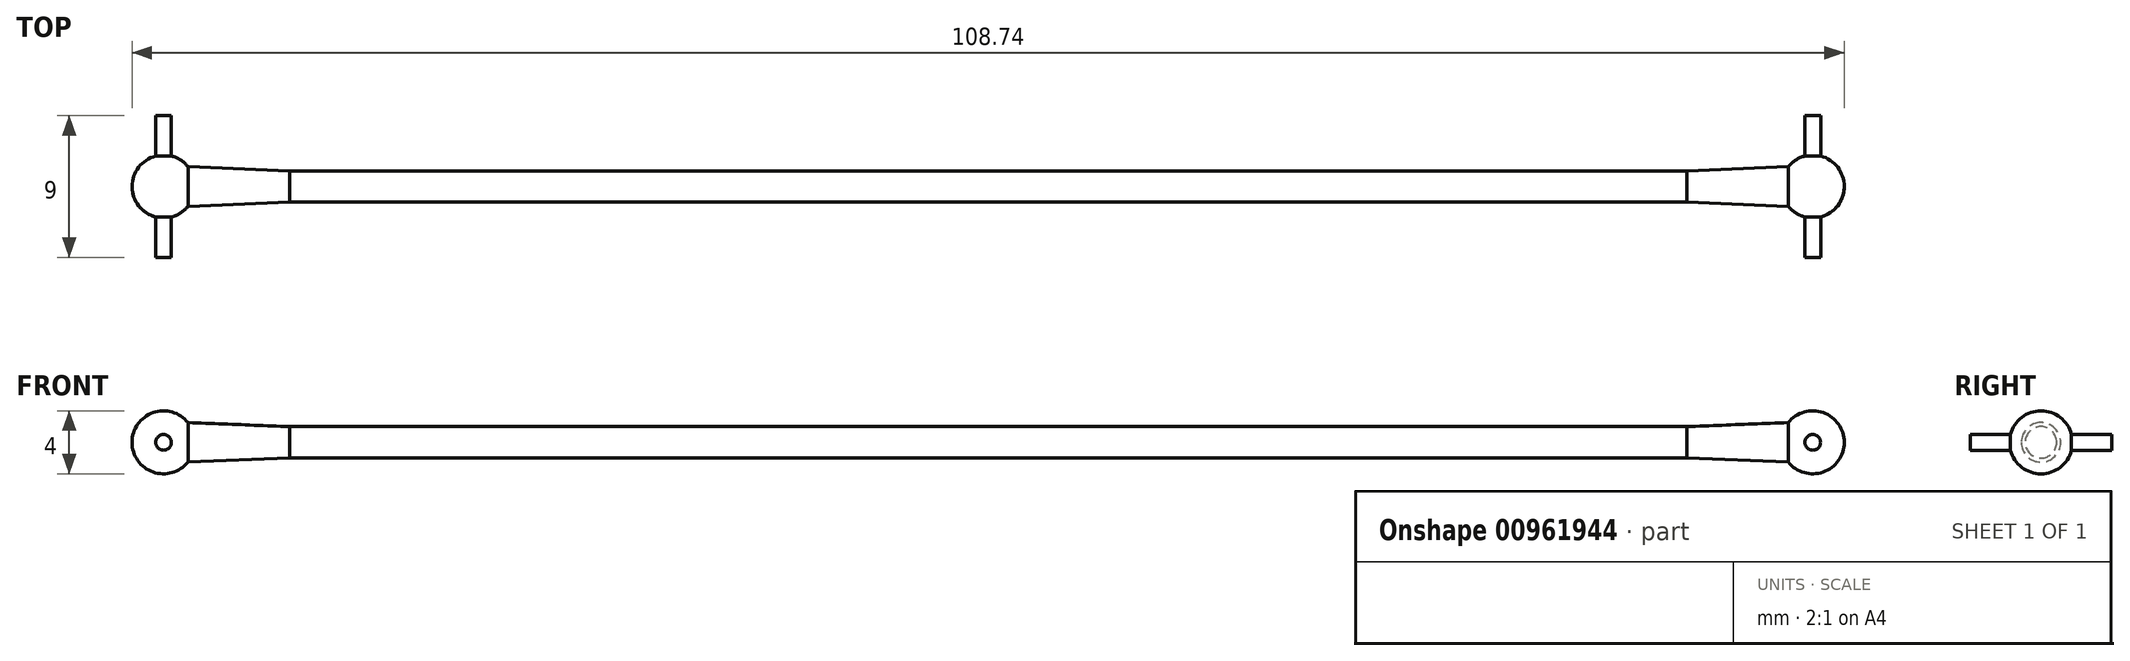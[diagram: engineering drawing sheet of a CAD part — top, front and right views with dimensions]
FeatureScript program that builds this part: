
annotation { "Feature Type Name" : "Feature", "Feature Type Description" : "" }
export const myFeature = defineFeature(function(context is Context, id is Id, definition is map)
    precondition{}
    {
        {
            var Q0;
            Q0=qCreatedBy(makeId("Top.planeOp"),FACE);
            var sketch = newSketch(context, id + "F0", { "sketchPlane" : qUnion([Q0])});
            skLineSegment(sketch, "E0.top", {"start": v(54.37, 0) * mm, "end": v(-54.37, 0) * mm});
            skPoint(sketch, "E0.middle", {"position": v(0, 0) * mm});
            skArc(sketch, "E1", {"start": v(-54.37, 0) * mm, "mid": v(-53.79, -1.41) * mm, "end": v(-52.37, -2) * mm});
            skArc(sketch, "E2", {"start": v(-50.37, 0) * mm, "mid": v(-50.96, -1.41) * mm, "end": v(-52.37, -2) * mm});
            skLineSegment(sketch, "E3", {"start": v(-50.82, -1.25) * mm, "end": v(-44.37, -1) * mm});
            skLineSegment(sketch, "E4.bottom", {"start": v(-51.87, 0) * mm, "end": v(-52.87, 0) * mm});
            skPoint(sketch, "E0.right.start.orphan", {"position": v(-54.37, 0) * mm});
            skLineSegment(sketch, "E5.MirrorCS", {"start": v(51.87, 0) * mm, "end": v(52.87, 0) * mm});
            skArc(sketch, "E6.MirrorCS", {"start": v(50.37, 0) * mm, "mid": v(50.96, -1.41) * mm, "end": v(52.37, -2) * mm});
            skArc(sketch, "E7.MirrorCS", {"start": v(54.37, 0) * mm, "mid": v(53.79, -1.41) * mm, "end": v(52.37, -2) * mm});
            skLineSegment(sketch, "E8.MirrorCS", {"start": v(-54.37, 0) * mm, "end": v(54.37, 0) * mm});
            skLineSegment(sketch, "E9.MirrorCS", {"start": v(50.82, -1.25) * mm, "end": v(44.37, -1) * mm});
            skLineSegment(sketch, "E10.trimOffspring", {"start": v(44.37, -1) * mm, "end": v(-44.37, -1) * mm});
            skPoint(sketch, "E0.left.start.orphan", {"position": v(54.37, 0) * mm});
            skLineSegment(sketch, "E11.trimOffspring", {"start": v(-44.37, -1) * mm, "end": v(44.37, -1) * mm});
            skLineSegment(sketch, "E12.bottom", {"start": v(52.37, 0) * mm, "end": v(51.87, 0) * mm});
            skLineSegment(sketch, "E12.top", {"start": v(52.37, 0) * mm, "end": v(51.87, 0) * mm});
            skLineSegment(sketch, "E12.left", {"start": v(52.37, 0) * mm, "end": v(52.37, 0) * mm});
            skLineSegment(sketch, "E12.right", {"start": v(51.87, 0) * mm, "end": v(51.87, 0) * mm});
            skSolve(sketch);
        }
        {
            var Q0;
            {var subQ4=sQuery(id+"F0.wireOp",EDGE,"E3");Q0=makeQuery(id+"F0.imprint","IMPRINT",FACE,{"disambiguationData":[TD([[makeQuery(id+"F0.imprint","IMPRINT",EDGE,{"derivedFrom":subQ4}),1.0]])]});}
            var Q1;
            {var subQ0=sQuery(id+"F0.wireOp",EDGE,"E8.MirrorCS");var subQ1=sQuery(id+"F0.wireOp",EDGE,"E2");var subQ2=makeQuery(id+"F0.imprint","INTERSECT",VERTEX,{"derivedFrom":[subQ1,subQ0]});Q1=makeQuery(id+"F0.imprint","IMPRINT",FACE,{"disambiguationData":[TD([[makeQuery(id+"F0.imprint","IMPRINT",EDGE,{"disambiguationData":[TD([[subQ2,-1.0]])],"derivedFrom":subQ1}),-1.0]])]});}
            var Q2;
            {var subQ0=sQuery(id+"F0.wireOp",EDGE,"E8.MirrorCS");var subQ5=sQuery(id+"F0.wireOp",EDGE,"E4.left");var subQ6=makeQuery(id+"F0.imprint","INTERSECT",VERTEX,{"derivedFrom":[subQ5,subQ0]});Q2=makeQuery(id+"F0.imprint","IMPRINT",FACE,{"disambiguationData":[TD([[makeQuery(id+"F0.imprint","IMPRINT",EDGE,{"disambiguationData":[TD([[subQ6,-1.0]])],"derivedFrom":subQ5}),-1.0]])]});}
            var Q3;
            {var subQ0=sQuery(id+"F0.wireOp",EDGE,"E8.MirrorCS");var subQ1=sQuery(id+"F0.wireOp",EDGE,"E1");var subQ2=makeQuery(id+"F0.imprint","INTERSECT",VERTEX,{"derivedFrom":[subQ1,subQ0]});Q3=makeQuery(id+"F0.imprint","IMPRINT",FACE,{"disambiguationData":[TD([[makeQuery(id+"F0.imprint","IMPRINT",EDGE,{"disambiguationData":[TD([[subQ2,-1.0]])],"derivedFrom":subQ1}),1.0]])]});}
            var Q4;
            {var subQ0=sQuery(id+"F0.wireOp",EDGE,"E8.MirrorCS");var subQ1=sQuery(id+"F0.wireOp",EDGE,"E7.MirrorCS");var subQ2=makeQuery(id+"F0.imprint","INTERSECT",VERTEX,{"derivedFrom":[subQ1,subQ0]});Q4=makeQuery(id+"F0.imprint","IMPRINT",FACE,{"disambiguationData":[TD([[makeQuery(id+"F0.imprint","IMPRINT",EDGE,{"disambiguationData":[TD([[subQ2,-1.0]])],"derivedFrom":subQ1}),-1.0]])]});}
            var Q5;
            {var subQ0=sQuery(id+"F0.wireOp",EDGE,"E8.MirrorCS");var subQ1=sQuery(id+"F0.wireOp",EDGE,"962a1150-f3b9-4dde-861a-ce8e05d1ab925.MirrorCS");var subQ2=makeQuery(id+"F0.imprint","INTERSECT",VERTEX,{"derivedFrom":[subQ1,subQ0]});Q5=makeQuery(id+"F0.imprint","IMPRINT",FACE,{"disambiguationData":[TD([[makeQuery(id+"F0.imprint","IMPRINT",EDGE,{"disambiguationData":[TD([[subQ2,-1.0]])],"derivedFrom":subQ1}),1.0]])]});}
            var Q6;
            {var subQ0=sQuery(id+"F0.wireOp",EDGE,"E8.MirrorCS");var subQ1=sQuery(id+"F0.wireOp",EDGE,"E6.MirrorCS");var subQ2=makeQuery(id+"F0.imprint","INTERSECT",VERTEX,{"derivedFrom":[subQ1,subQ0]});Q6=makeQuery(id+"F0.imprint","IMPRINT",FACE,{"disambiguationData":[TD([[makeQuery(id+"F0.imprint","IMPRINT",EDGE,{"disambiguationData":[TD([[subQ2,-1.0]])],"derivedFrom":subQ1}),1.0]])]});}
            var Q7;
            {var subQ1=sQuery(id+"F0.wireOp",EDGE,"E2");var subQ3=sQuery(id+"F0.wireOp",EDGE,"2c2fce1d-def3-4a14-a7ae-c48ec30f6c030.MirrorCS");var subQ4=makeQuery(id+"F0.imprint","INTERSECT",VERTEX,{"derivedFrom":[subQ1,subQ3]});Q7=makeQuery(id+"F0.imprint","IMPRINT",FACE,{"disambiguationData":[TD([[makeQuery(id+"F0.imprint","IMPRINT",EDGE,{"disambiguationData":[TD([[subQ4,-1.0]])],"derivedFrom":subQ1}),-1.0]])]});}
            var Q8;
            {var subQ5=sQuery(id+"F0.wireOp",EDGE,"E12.bottom");Q8=makeQuery(id+"F0.imprint","IMPRINT",FACE,{"disambiguationData":[TD([[makeQuery(id+"F0.imprint","IMPRINT",EDGE,{"derivedFrom":subQ5}),1.0]])]});}
            var Q9;
            Q9=sQuery(id+"F0.wireOp",EDGE,"E8.MirrorCS");
            revolve(context, id + "F1", {"surfaceOperationType" : NewSurfaceOperationType.NEW, "entities" : qUnion([Q0, Q1, Q2, Q3, Q4, Q5, Q6, Q7, Q8]), "axis" : qUnion([Q9]), "revolveType" : RevolveType.FULL});
        }
        {
            var Q0;
            Q0=qCreatedBy(makeId("Front.planeOp"),FACE);
            var sketch = newSketch(context, id + "F2", { "sketchPlane" : qUnion([Q0])});
            skArc(sketch, "E13", {"start": v(-50.82, 1.25) * mm, "mid": v(-54.37, 0) * mm, "end": v(-50.82, -1.25) * mm});
            skCircle(sketch, "E14", {"center": v(-52.37, 0) * mm, "radius": 0.5 * mm});
            skSolve(sketch);
        }
        {
            var Q0;
            Q0 = qSketchRegion(id + "F2", true);
            extrude(context, id + "F3", {"entities" : qUnion([Q0]), "operationType" : NewBodyOperationType.ADD, "depth" : 9 * mm, "offsetDistance" : 25 * mm, "symmetric" : true});
        }
        {
            var Q0;
            Q0=qCreatedBy(makeId("Front.planeOp"),FACE);
            var sketch = newSketch(context, id + "F4", { "sketchPlane" : qUnion([Q0])});
            skArc(sketch, "E15", {"start": v(50.82, -1.25) * mm, "mid": v(54.37, 0) * mm, "end": v(50.82, 1.25) * mm});
            skCircle(sketch, "E16", {"center": v(52.37, 0) * mm, "radius": 0.5 * mm});
            skSolve(sketch);
        }
        {
            var Q0;
            Q0 = qSketchRegion(id + "F4", true);
            extrude(context, id + "F5", {"entities" : qUnion([Q0]), "operationType" : NewBodyOperationType.ADD, "depth" : 9 * mm, "offsetDistance" : 25 * mm, "symmetric" : true});
        }
    });
